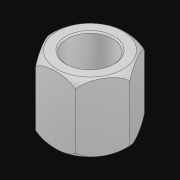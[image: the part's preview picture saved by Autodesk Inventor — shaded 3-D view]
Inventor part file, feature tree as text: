
AUTODESK INVENTOR PART (.ipt)
format: ipt  version: 2021.3 (Build 253353010, 353A)  size: 205,824 bytes
history: native  units: in
note: dims shown in document units (in); Inventor stores cm internally (conversion verified against a paired STEP export)
features: other x12, sketch x6, chamfer x3, hole x3, extrude x2
ambient origin geometry x8: Origin, YZ Plane, XZ Plane, XY Plane, X Axis, Y Axis, Z Axis, Center Point
bodies: Solid1 (feature_tree), Body (feature_tree)
feature tree (26):
  other  "Table"
  other  "Standoff .25"
  other  "Standoff .50"
  other  "Standoff .75"
  other  "Standoff 1.00"
  other  "Standoff 1.50"
  other  "Standoff 2.00"
  other  "Standoff 2.50"
  other  "Standoff 3.00"
  other  "Standoff 4.00"
  other  "Standoff 5.00"
  other  "Standoff 6.00"
  extrude  "Hole 2"  TaperAngle=0.0deg  [1 undecoded]
  extrude  "Hole 1"  Depth=0.5in TaperAngle=0.0deg
  chamfer  "Hole 2 Chamfer 1"  Distance=0.5in
  chamfer  "Hole 1 Chamfer 1"  Distance=0.005in Angle=45.0deg
  hole  "Hole 2 Chamfer 2"  [1 undecoded]
  hole  "Hole 1 Chamfer 2"  [1 undecoded]
  chamfer  "Hole 2 Chamfer 1 For Short"  Distance=0.1195in
  hole  "Hole 2 Chamfer 2 For Short"  [1 undecoded]
  sketch  "Sketch1"  dims[d0=0.25in d2=0.0in]
  sketch  "Sketch2"  dims[d3=0.165in d4=0.5in d5=0.0in]
  sketch  "Sketch3"  dims[d6=0.165in d7=0.5in d8=0.0in d9=0.005in d10=0.0049in d11=45.0deg]
  sketch  "Sketch4"  dims[d12=0.005in d13=0.0049in d14=45.0deg d15=0.1195in]
  sketch  "Sketch5"  dims[d16=0.065in d17=0.025in]
  sketch  "Sketch7"  dims[d18=90.0deg d19=0.1195in d20=0.065in d21=0.025in d22=90.0deg d30=0.005in d31=0.0049in d32=45.0deg d33=0.1195in d34=0.065in d35=0.025in d36=90.0deg]
note: 4 required parameter values undecoded (feature->parameter linkage not recoverable at this tier; creation-order binding heuristic only, values carry confidence <= 0.55)
